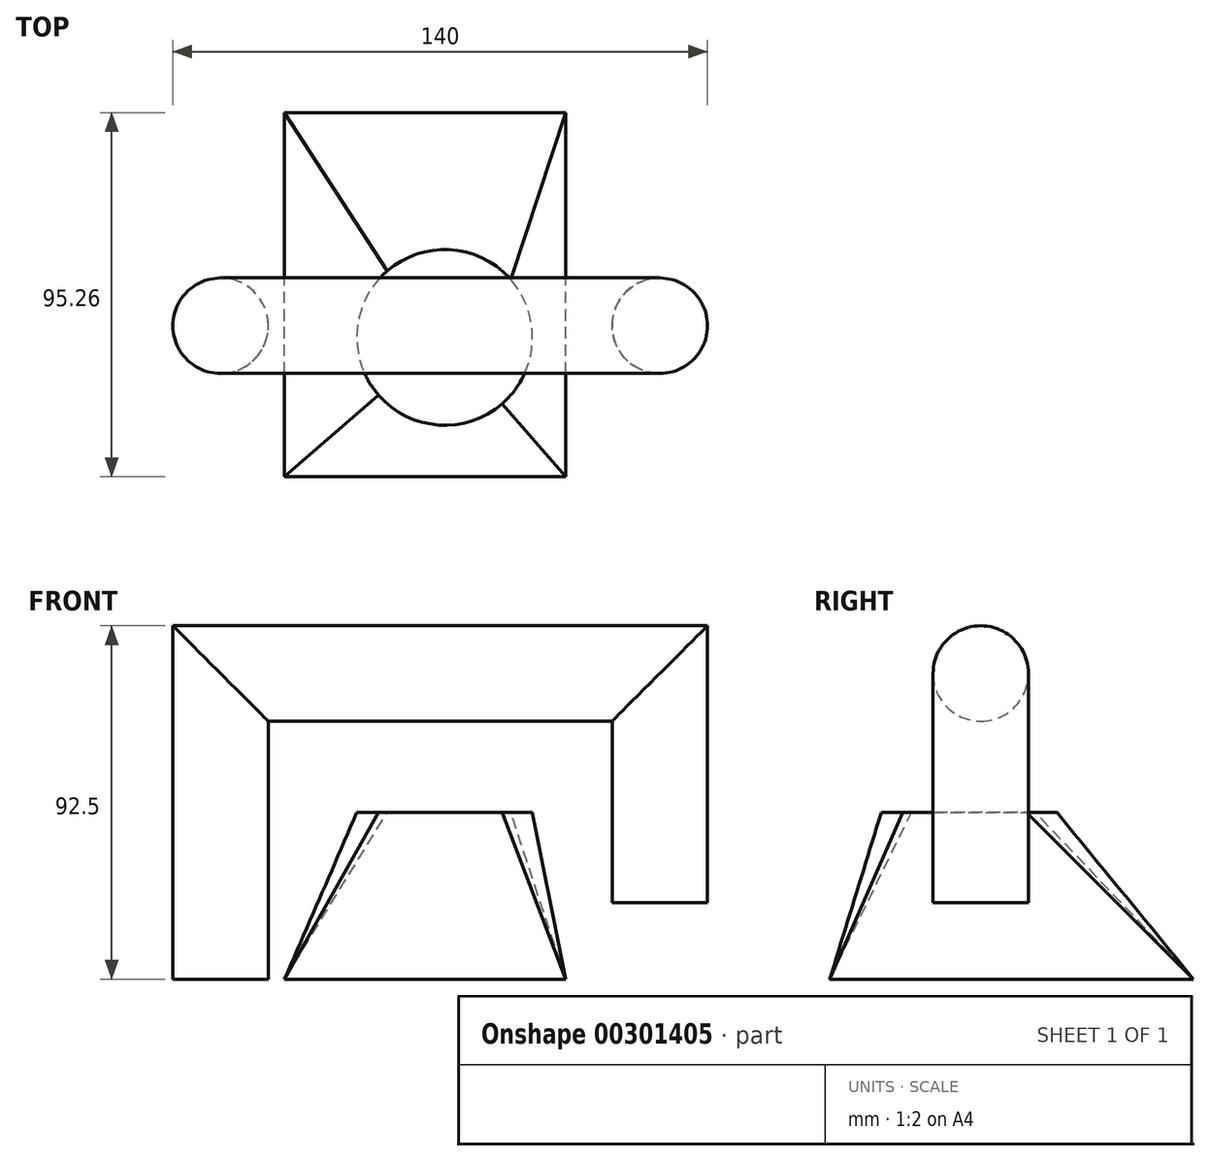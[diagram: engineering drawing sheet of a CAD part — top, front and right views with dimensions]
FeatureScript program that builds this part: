
annotation { "Feature Type Name" : "Feature", "Feature Type Description" : "" }
export const myFeature = defineFeature(function(context is Context, id is Id, definition is map)
    precondition{}
    {
        {
            var Q0;
            Q0=qCreatedBy(makeId("Top.planeOp"),FACE);
            var sketch = newSketch(context, id + "F0", { "sketchPlane" : qUnion([Q0])});
            skCircle(sketch, "E0", {"center": v(0, 0) * mm, "radius": 12.5 * mm});
            skSolve(sketch);
        }
        {
            var Q0;
            Q0=qCreatedBy(makeId("Front.planeOp"),FACE);
            var sketch = newSketch(context, id + "F1", { "sketchPlane" : qUnion([Q0])});
            skLineSegment(sketch, "E1", {"start": v(0, 0) * mm, "end": v(0, 80) * mm});
            skLineSegment(sketch, "E2", {"start": v(0, 80) * mm, "end": v(115, 80) * mm});
            skLineSegment(sketch, "E3", {"start": v(115, 80) * mm, "end": v(115, 20) * mm});
            skSolve(sketch);
        }
        {
            var Q0;
            Q0=makeQuery(id+"F0.imprint","IMPRINT",FACE,{"disambiguationData":[TD([[makeQuery(id+"F0.imprint","IMPRINT",EDGE,{"derivedFrom":sQuery(id+"F0.wireOp",EDGE,"E0")}),1.0]])]});
            var Q1;
            Q1=sQuery(id+"F1.wireOp",EDGE,"E1");
            var Q2;
            Q2=sQuery(id+"F1.wireOp",EDGE,"E2");
            var Q3;
            Q3=sQuery(id+"F1.wireOp",EDGE,"E3");
            sweep(context, id + "F2", {"profiles" : qUnion([Q0]), "path" : qUnion([Q1, Q2, Q3])});
        }
        {
            var Q0;
            Q0=qCreatedBy(makeId("Top.planeOp"),FACE);
            var sketch = newSketch(context, id + "F3", { "sketchPlane" : qUnion([Q0])});
            skLineSegment(sketch, "E4.bottom", {"start": v(16.75, -39.53) * mm, "end": v(90.4, -39.53) * mm});
            skLineSegment(sketch, "E4.top", {"start": v(16.75, 55.73) * mm, "end": v(90.4, 55.73) * mm});
            skLineSegment(sketch, "E4.left", {"start": v(16.75, -39.53) * mm, "end": v(16.75, 55.73) * mm});
            skLineSegment(sketch, "E4.right", {"start": v(90.4, -39.53) * mm, "end": v(90.4, 55.73) * mm});
            skSolve(sketch);
        }
        {
            var Q0;
            Q0=qCreatedBy(makeId("Top.planeOp"),FACE);
            cPlane(context, id + "F4", {"entities" : qUnion([Q0]), "cplaneType" : CPlaneType.OFFSET, "offset" : 43.6 * mm, "width" : 150 * mm, "height" : 150 * mm});
        }
        {
            var Q0;
            Q0=qCreatedBy(id+"F4.planeOp",FACE);
            var sketch = newSketch(context, id + "F5", { "sketchPlane" : qUnion([Q0])});
            skCircle(sketch, "E5", {"center": v(58.66, -3.06) * mm, "radius": 22.99 * mm});
            skSolve(sketch);
        }
        {
            var Q0;
            Q0=makeQuery(id+"F3.imprint","IMPRINT",FACE,{"disambiguationData":[TD([[makeQuery(id+"F3.imprint","IMPRINT",EDGE,{"derivedFrom":sQuery(id+"F3.wireOp",EDGE,"E4.bottom")}),1.0]])]});
            var Q1;
            Q1=makeQuery(id+"F5.imprint","IMPRINT",FACE,{"disambiguationData":[TD([[makeQuery(id+"F5.imprint","IMPRINT",EDGE,{"derivedFrom":sQuery(id+"F5.wireOp",EDGE,"E5")}),1.0]])]});
            loft(context, id + "F6", {"sheetProfilesArray" : [{ "sheetProfileEntities" : qUnion([Q0]) }, { "sheetProfileEntities" : qUnion([Q1]) }]});
        }
    });
